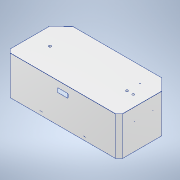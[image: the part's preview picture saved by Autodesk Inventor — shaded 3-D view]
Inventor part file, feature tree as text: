
AUTODESK INVENTOR PART (.ipt)
format: ipt  version: 2022 (Build 260153000, 153)  size: 707,584 bytes
history: native  units: mm
features: other x42, sketch x12, projected_geometry x11, reference x3, plane x2, hole x2, extrude x2
ambient origin geometry x8: Origin, YZ Plane, XZ Plane, XY Plane, X Axis, Y Axis, Z Axis, Center Point
bodies: Body1 (feature_tree)
feature tree (74):
  other  "Sólido1"
  other  "Cara1"
  sketch  "Boceto2"  dims[d2=34.0mm d3=34.0mm]
  other  "Cara2"
  other  "Cara3"
  other  "Doblez3"
  other  "Cara4"
  sketch  "Boceto6"  dims[d8=373.081mm]
  plane  "Plano de trabajo2"
  plane  "Plano de trabajo1"
  other  "Cara11"
  other  "Cara12"
  other  "Cara13"
  hole  "Agujero2"  [1 undecoded]
  hole  "Agujero1"  [1 undecoded]
  other  "Cara14"
  other  "Cara15"
  extrude  "Extrusión1"  Depth=34.0mm
  extrude  "Extrusión3"  Depth=0.5mm
  sketch  "Boceto1"  dims[d0=1085.0mm d1=525.0mm]
  other  "Placa1"
  projected_geometry  "Contorno proyectado1"
  projected_geometry  "Contorno proyectado2"
  projected_geometry  "Contorno proyectado3"
  other  "Placa2"
  other  "Doblez1"
  sketch  "Boceto4"  dims[d4=380.0mm d5=34.0mm]
  projected_geometry  "Contorno proyectado4"
  other  "Placa3"
  other  "Doblez2"
  sketch  "Boceto5"  dims[d6=860.0mm d7=0.5mm]
  projected_geometry  "Contorno proyectado5"
  projected_geometry  "Contorno proyectado6"
  projected_geometry  "Contorno proyectado7"
  projected_geometry  "Contorno proyectado8"
  other  "Placa4"
  other  "Doblez4"
  projected_geometry  "Contorno proyectado9"
  projected_geometry  "Contorno proyectado10"
  sketch  "Boceto11"  dims[d9=0.5mm]
  reference  "Referencia2"
  sketch  "Boceto13"  dims[d10=0.5mm]
  reference  "Referencia3"
  reference  "Referencia4"
  other  "Placa11"
  other  "Doblez21"
  sketch  "Boceto15"  dims[d11=0.25mm]
  other  "Placa12"
  other  "Doblez22"
  sketch  "Boceto16"  dims[d12=1.0mm]
  other  "Placa13"
  other  "Doblez23"
  sketch  "Boceto17"  dims[d13=0.5mm]
  other  "Placa14"
  other  "Doblez24"
  sketch  "Boceto18"  dims[d14=0.5mm]
  other  "Placa15"
  other  "Doblez25"
  sketch  "Boceto21"  dims[d15=0.5mm d16=0.25mm d17=1.0mm d18=0.5mm d19=0.5mm d20=0.25mm d21=1.0mm d22=0.5mm d23=0.5mm d24=0.5mm d25=0.5mm d26=0.25mm d27=1.0mm d28=0.5mm d94=80.0mm d95=309.765299mm d96=0.5mm d97=0.0mm d98=100.0mm d99=40.0mm d105=0.5mm d106=0.0mm d107=5.0mm d108=5.0mm d109=3.4mm d110=7.01mm d111=6.3mm d112=2.0mm d113=90.0deg d114=0.5mm d115=20.594885mm d116=3.4mm d117=6.0mm d118=4.0mm d119=2.0mm d120=90.0deg d121=8.0mm d122=20.594885mm d134=0.5mm d135=0.5mm d136=0.25mm d137=1.0mm d138=0.5mm d139=47.0mm d140=0.5mm d141=0.5mm d142=0.25mm d143=1.0mm d144=0.5mm d145=47.0mm d146=0.5mm d147=0.5mm d148=0.25mm d149=1.0mm d150=0.5mm d151=2.0mm d152=0.5mm d153=0.5mm d154=0.0mm d155=10.0mm d156=2.0mm d157=0.5mm d158=0.5mm d159=0.0mm d160=10.0mm d161=157.0mm d162=0.5mm d163=0.5mm d164=0.25mm d165=1.0mm d166=0.5mm d167=157.0mm d168=0.5mm d169=0.5mm d170=0.25mm d171=1.0mm d172=0.5mm d173=2.0mm d174=0.5mm d175=0.5mm d176=0.0mm d177=10.0mm d178=2.0mm d179=0.5mm d180=0.5mm d181=0.0mm d182=10.0mm d183=80.0mm d184=80.0mm d185=210.0mm d187=22.0mm d192=12.7mm d193=17.0mm d194=247.109993mm d195=100.0mm d196=40.0mm d197=10.0mm d198=0.0mm d199=5.5mm d200=6.1mm d201=125.0mm d202=19.0mm d216=298.085786mm d217=35.0mm d218=4.5mm d219=2.5mm d220=1.1mm d221=10.0mm d222=10.0mm d223=2.4mm d224=2.4mm d225=10.0mm d226=0.0mm]
  projected_geometry  "Contorno proyectado22"
  other  "Esquina1"
  other  "Esquina2"
  other  "Cortar1"
  other  "Cortar2"
  other  "Esquina3"
  other  "Esquina4"
  other  "<userpath>\Desktop\PDM\ProyectoRobotPallet\RobotPallet.iam"
  other  "RobotPallet.iam"
  other  "EstructuraInferior - Soldadura:1"
  other  "Frame_Base:1"
  other  "ISO 10799-2 40x40x2 - 2899.41:1"
  other  "ISO 4762 M3 x 16:5"
  other  "ISO 4762 M3 x 16:6"
  other  "Definición1"
note: 2 required parameter values undecoded (feature->parameter linkage not recoverable at this tier; creation-order binding heuristic only, values carry confidence <= 0.55)
